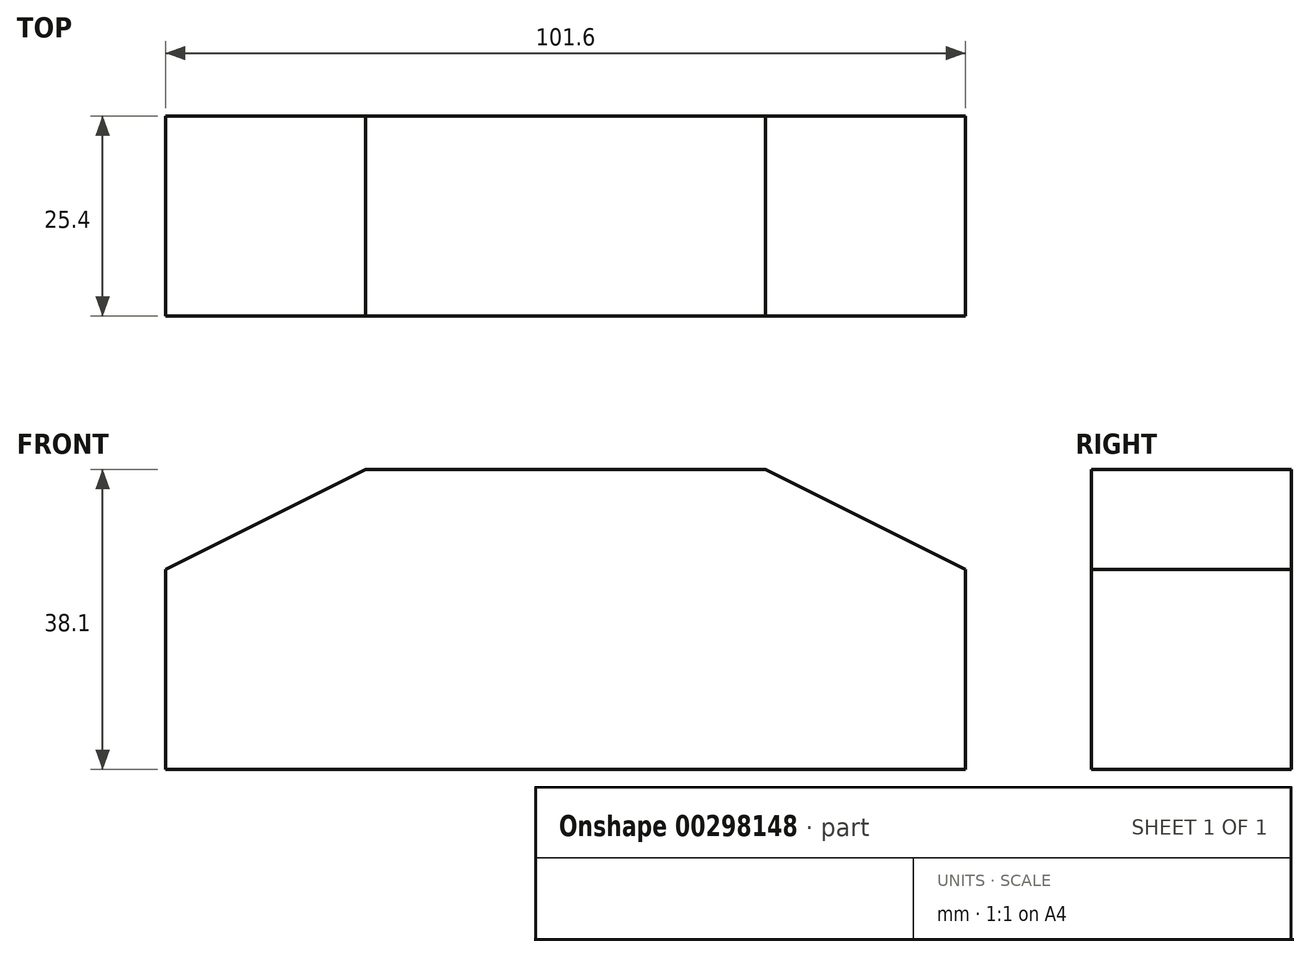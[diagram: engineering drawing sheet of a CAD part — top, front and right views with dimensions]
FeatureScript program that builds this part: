
annotation { "Feature Type Name" : "Feature", "Feature Type Description" : "" }
export const myFeature = defineFeature(function(context is Context, id is Id, definition is map)
    precondition{}
    {
        {
            var Q0;
            Q0=qCreatedBy(makeId("Front.planeOp"),FACE);
            var sketch = newSketch(context, id + "F0", { "sketchPlane" : qUnion([Q0])});
            skLineSegment(sketch, "E0.bottom", {"start": v(50.8, -12.7) * mm, "end": v(-50.8, -12.7) * mm});
            skLineSegment(sketch, "E0.top", {"start": v(50.8, 12.7) * mm, "end": v(-50.8, 12.7) * mm});
            skLineSegment(sketch, "E0.left", {"start": v(50.8, -12.7) * mm, "end": v(50.8, 12.7) * mm});
            skLineSegment(sketch, "E0.right", {"start": v(-50.8, -12.7) * mm, "end": v(-50.8, 12.7) * mm});
            skPoint(sketch, "E0.middle", {"position": v(0, 0) * mm});
            skLineSegment(sketch, "E1.bottom", {"start": v(-25.4, 12.7) * mm, "end": v(25.4, 12.7) * mm});
            skLineSegment(sketch, "E1.top", {"start": v(-25.4, 25.4) * mm, "end": v(25.4, 25.4) * mm});
            skLineSegment(sketch, "E1.left", {"start": v(-25.4, 12.7) * mm, "end": v(-25.4, 25.4) * mm});
            skLineSegment(sketch, "E1.right", {"start": v(25.4, 12.7) * mm, "end": v(25.4, 25.4) * mm});
            skPoint(sketch, "E1.middle", {"position": v(0, 19.05) * mm});
            skLineSegment(sketch, "E2", {"start": v(-25.4, 25.4) * mm, "end": v(-50.8, 12.7) * mm});
            skLineSegment(sketch, "E3", {"start": v(25.4, 25.4) * mm, "end": v(50.8, 12.7) * mm});
            skSolve(sketch);
        }
        {
            var Q0;
            Q0 = qSketchRegion(id + "F0", true);
            extrude(context, id + "F1", {"entities" : qUnion([Q0]), "depth" : 25.4 * mm});
        }
    });
